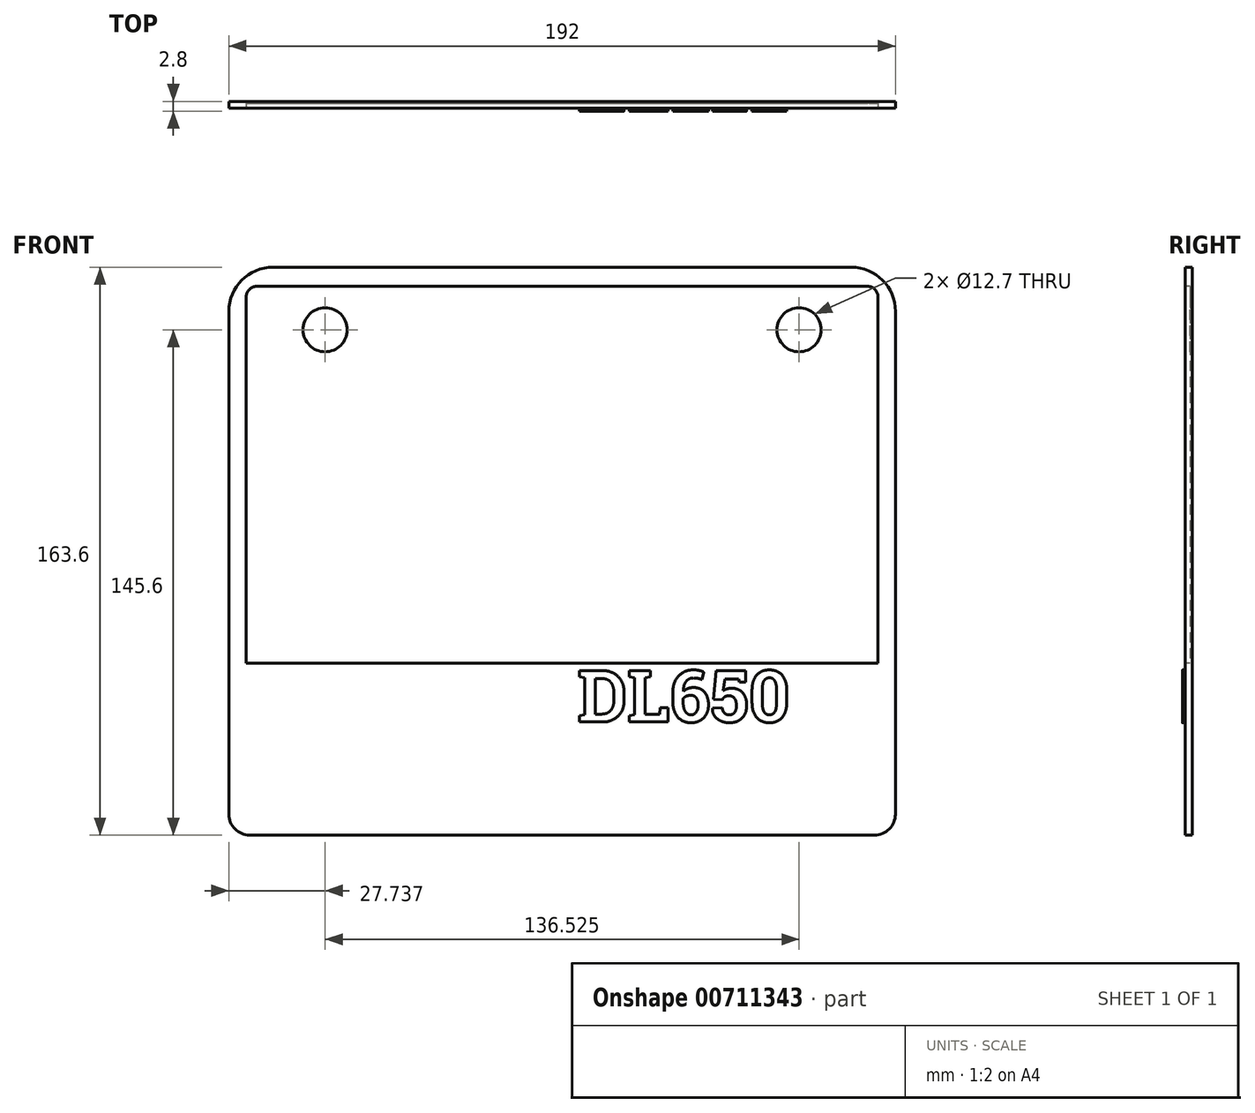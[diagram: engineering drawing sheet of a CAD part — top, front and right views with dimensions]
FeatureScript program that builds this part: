
annotation { "Feature Type Name" : "Feature", "Feature Type Description" : "" }
export const myFeature = defineFeature(function(context is Context, id is Id, definition is map)
    precondition{}
    {
        {
            var Q0;
            Q0=qCreatedBy(makeId("Front.planeOp"),FACE);
            var sketch = newSketch(context, id + "F0", { "sketchPlane" : qUnion([Q0])});
            skLineSegment(sketch, "E0", {"start": v(-83.3, 78) * mm, "end": v(83.3, 78) * mm});
            skLineSegment(sketch, "E1", {"start": v(-96, -23.6) * mm, "end": v(-96, 65.3) * mm});
            skLineSegment(sketch, "E2", {"start": v(96, 65.3) * mm, "end": v(96, -23.6) * mm});
            skCircle(sketch, "E3", {"center": v(-68.26, 60) * mm, "radius": 6.35 * mm});
            skCircle(sketch, "E4", {"center": v(68.26, 60) * mm, "radius": 6.35 * mm});
            skArc(sketch, "E5", {"start": v(-83.3, 78) * mm, "mid": v(-92.28, 74.28) * mm, "end": v(-96, 65.3) * mm});
            skArc(sketch, "E6", {"start": v(96, 65.3) * mm, "mid": v(92.28, 74.28) * mm, "end": v(83.3, 78) * mm});
            skLineSegment(sketch, "E7", {"start": v(-96, -23.6) * mm, "end": v(96, -23.6) * mm});
            skLineSegment(sketch, "E8", {"start": v(0, 78) * mm, "end": v(0, 44.35) * mm, "construction": true});
            skLineSegment(sketch, "E9", {"start": v(0, 0) * mm, "end": v(0, -23.6) * mm, "construction": true});
            skLineSegment(sketch, "E10", {"start": v(0, 44.35) * mm, "end": v(-96, 44.35) * mm, "construction": true});
            skLineSegment(sketch, "E11", {"start": v(0, 44.35) * mm, "end": v(96, 44.35) * mm, "construction": true});
            skSolve(sketch);
        }
        {
            var Q0;
            Q0=qSketchRegion(id+"F0",true);
            extrude(context, id + "F1", {"entities" : qUnion([Q0]), "depth" : 2 * mm, "offsetDistance" : 25 * mm});
        }
        {
            var Q0;
            Q0=makeQuery(id+"F1.opExtrude","CAP_FACE",FACE,{"disambiguationData":[OSD([sQuery(id+"F0.wireOp",EDGE,"E0"),sQuery(id+"F0.wireOp",EDGE,"48a6f060-a1ac-46d0-8047-a4f0a9823539"),sQuery(id+"F0.wireOp",EDGE,"E1"),sQuery(id+"F0.wireOp",EDGE,"E2"),sQuery(id+"F0.wireOp",EDGE,"f30ca258-66be-4d38-bb74-7f78c57f1080"),sQuery(id+"F0.wireOp",EDGE,"45272e1f-5984-409b-a4f0-3096130aef37"),sQuery(id+"F0.wireOp",EDGE,"648265e5-3534-4ccd-a4d5-83f80079090c"),sQuery(id+"F0.wireOp",EDGE,"c0985e6e-a1f7-4fb3-8751-1b5ac6839632"),sQuery(id+"F0.wireOp",EDGE,"e40d4cf7-7397-40ef-a449-90f8d66566dd"),sQuery(id+"F0.wireOp",EDGE,"e08eb2a6-f8ba-4677-9665-afa96b0a5c42"),sQuery(id+"F0.wireOp",EDGE,"e09e89fb-475b-45c4-a03c-8bf25691b274"),sQuery(id+"F0.wireOp",EDGE,"c3a1d90c-5dae-4514-9c18-9578f9fa1c24"),sQuery(id+"F0.wireOp",EDGE,"de0bfc80-6dc8-401c-842a-22218dc18f48"),sQuery(id+"F0.wireOp",EDGE,"10bace14-cf57-4a17-8dbc-91b2d8cd16bf"),sQuery(id+"F0.wireOp",EDGE,"deb3eb6b-2df6-45dd-ab49-f1686ca42383"),sQuery(id+"F0.wireOp",EDGE,"6de70d99-d249-41b2-88aa-bb0862796ce5"),sQuery(id+"F0.wireOp",EDGE,"b2971fcf-4c8f-4d95-a7b3-968699cf8065"),sQuery(id+"F0.wireOp",EDGE,"79488e33-7403-455a-a2d1-9183c7a7dc75"),sQuery(id+"F0.wireOp",EDGE,"aa5a9b35-dc5f-46a3-a21f-bc2f6a5ba8c3"),sQuery(id+"F0.wireOp",EDGE,"64001aba-4a60-4bdb-a6e0-b909cfa90190"),sQuery(id+"F0.wireOp",EDGE,"69a3c832-ee76-48c3-8be5-449944f03f95"),sQuery(id+"F0.wireOp",EDGE,"49a81c46-1861-4f30-adb0-815aeb534458"),sQuery(id+"F0.wireOp",EDGE,"e41367db-3de3-4109-90ef-63e5f0f7b1f7"),sQuery(id+"F0.wireOp",EDGE,"6e4c30f9-b3e7-4410-98fe-95563731d562"),sQuery(id+"F0.wireOp",EDGE,"50d6a7da-0eb8-46df-9db0-2777529e0e33"),sQuery(id+"F0.wireOp",EDGE,"8f5f6bae-5651-4266-a81d-530af63d2ea9"),sQuery(id+"F0.wireOp",EDGE,"0c91ba03-d5dc-41c7-8701-761e688114d9"),sQuery(id+"F0.wireOp",EDGE,"10e95849-eba9-4293-a9a6-05e2b37bbdfd"),sQuery(id+"F0.wireOp",EDGE,"edf70701-9639-44fa-8111-f0ba9ba4bb0e"),sQuery(id+"F0.wireOp",EDGE,"9cb7c61f-063f-4e49-a479-e91a873714ef"),sQuery(id+"F0.wireOp",EDGE,"23d4df54-0a09-4bbe-b8b9-fc41ac67f4ac"),sQuery(id+"F0.wireOp",EDGE,"d0cc7293-f9a2-43ae-ac4b-742a364b32c0"),sQuery(id+"F0.wireOp",EDGE,"1dbc8700-6e9f-4588-83ba-0a038fd47aa9"),sQuery(id+"F0.wireOp",EDGE,"171cbcd0-81c7-4dfe-8efe-28eec8b9f1e2"),sQuery(id+"F0.wireOp",EDGE,"1b840b68-42d4-491e-8676-f044272edf1d"),sQuery(id+"F0.wireOp",EDGE,"477a06df-0e00-41ca-87d7-5c34f2a07242"),sQuery(id+"F0.wireOp",EDGE,"7aeb2e31-d47a-4962-ad1a-87ad22c54afe"),sQuery(id+"F0.wireOp",EDGE,"8aeabe10-1c55-41c1-b53d-efc54e2343e8"),sQuery(id+"F0.wireOp",EDGE,"56056688-4674-4c79-9f3a-c66bce5d7240"),sQuery(id+"F0.wireOp",EDGE,"2ba6e904-2303-4a58-a2cc-d8b69b776228"),sQuery(id+"F0.wireOp",EDGE,"5e924ffd-c203-416b-82ef-407f079c669c"),sQuery(id+"F0.wireOp",EDGE,"22999e4d-675b-4f8e-a222-469bac07e6be"),sQuery(id+"F0.wireOp",EDGE,"8f11fb03-c33d-4eef-9f43-5a4f08b6129f"),sQuery(id+"F0.wireOp",EDGE,"a5862e19-85fe-4436-8071-eee2bcb2075c"),sQuery(id+"F0.wireOp",EDGE,"ed11b90d-34d2-40d8-97b3-85c497fa4b90"),sQuery(id+"F0.wireOp",EDGE,"8821150d-f62d-464a-944b-e17730e76b97"),sQuery(id+"F0.wireOp",EDGE,"73421591-e8bf-419b-8db1-77e700152255"),sQuery(id+"F0.wireOp",EDGE,"55a8d366-2669-4621-9984-ea7371f670e7"),sQuery(id+"F0.wireOp",EDGE,"fca3974c-c5bd-4598-b391-3bcec77630d6"),sQuery(id+"F0.wireOp",EDGE,"1c73d825-d1c4-4b0e-8cd0-2f197b32ed0e"),sQuery(id+"F0.wireOp",EDGE,"f12474dd-ca9d-467a-b6b7-96876f0ada5b"),sQuery(id+"F0.wireOp",EDGE,"ffd498c9-8f44-4c4b-88ae-d53ebce42681"),sQuery(id+"F0.wireOp",EDGE,"d78736cb-32b1-4983-8c7f-334d7760df66"),sQuery(id+"F0.wireOp",EDGE,"95740ca0-fcd5-4cb7-9504-a285a5dde6e3"),sQuery(id+"F0.wireOp",EDGE,"ebb5eec3-1149-4952-a6d1-94870ff9836f"),sQuery(id+"F0.wireOp",EDGE,"09364745-caed-4ffe-8d3c-952926bc9417"),sQuery(id+"F0.wireOp",EDGE,"a9181265-9252-4b23-9b63-f6bef6a5911b"),sQuery(id+"F0.wireOp",EDGE,"a53fe2a5-8e1d-4d15-8c4a-13980fa5923c"),sQuery(id+"F0.wireOp",EDGE,"9b227ee3-73b3-485d-a44c-8cd02b23a3f0"),sQuery(id+"F0.wireOp",EDGE,"062db7e1-9f89-4046-92a1-9e257b0f6c50"),sQuery(id+"F0.wireOp",EDGE,"351c1721-7ed2-435b-ad4a-6d0b63d51eff"),sQuery(id+"F0.wireOp",EDGE,"71a8f4bf-e319-473b-8b4e-3c091c66e44c"),sQuery(id+"F0.wireOp",EDGE,"c68ce1a5-2e28-4d52-a029-c52856a99a74"),sQuery(id+"F0.wireOp",EDGE,"561223bc-eb1b-49aa-80b6-663cd7c405cc"),sQuery(id+"F0.wireOp",EDGE,"4449a819-5709-48c0-965c-65add78f8043"),sQuery(id+"F0.wireOp",EDGE,"a0f13820-d3c8-4b17-b0b8-00fd948fe85f"),sQuery(id+"F0.wireOp",EDGE,"20fca5f8-8561-4aa7-a30f-3738d70a8836"),sQuery(id+"F0.wireOp",EDGE,"920726d8-d7a8-4d7b-bd5a-44d794fb4a9e"),sQuery(id+"F0.wireOp",EDGE,"a76c174e-0144-4079-be69-9e1200ad9bf8"),sQuery(id+"F0.wireOp",EDGE,"98b53387-61df-4284-a1fd-1e532390bc76"),sQuery(id+"F0.wireOp",EDGE,"7970af7d-46bf-4ec9-b671-f062ccba2269"),sQuery(id+"F0.wireOp",EDGE,"6e09d304-04a0-4725-848f-3effe17a6afc"),sQuery(id+"F0.wireOp",EDGE,"3df50d65-f073-4170-bc94-899382cb2db7"),sQuery(id+"F0.wireOp",EDGE,"ec83f8f2-8803-4207-88f9-0d4175c8ecd2"),sQuery(id+"F0.wireOp",EDGE,"2f88a13a-97f7-4f31-871f-ef8b0bef47c0"),sQuery(id+"F0.wireOp",EDGE,"06910b89-3a32-40f6-98a8-ac0792bcf854"),sQuery(id+"F0.wireOp",EDGE,"1496428c-a744-4ad0-9076-c4c48af7c995"),sQuery(id+"F0.wireOp",EDGE,"cc24b7ec-eed3-4d97-bc37-77a5319da4e8"),sQuery(id+"F0.wireOp",EDGE,"f009715c-78f4-41d5-a120-40e9715128f4"),sQuery(id+"F0.wireOp",EDGE,"5595ca81-0dc4-4751-825f-2c64607c6bfd"),sQuery(id+"F0.wireOp",EDGE,"75137ea1-8823-43c0-92ee-8dea83bb2410"),sQuery(id+"F0.wireOp",EDGE,"f83aa6e6-86ae-462f-9473-6b6f0fb29268"),sQuery(id+"F0.wireOp",EDGE,"d90fdb54-86cb-4136-93d7-04ef30efafac"),sQuery(id+"F0.wireOp",EDGE,"8bd12bbf-22fc-44f8-9b72-60e51806dfd9"),sQuery(id+"F0.wireOp",EDGE,"d2235da4-86d1-4fb2-9421-07340d50dd9e"),sQuery(id+"F0.wireOp",EDGE,"63672669-45e7-48f5-b998-5c0e149c1244"),sQuery(id+"F0.wireOp",EDGE,"58c0fe2c-0100-4913-a047-5c3918bec01d"),sQuery(id+"F0.wireOp",EDGE,"41e70165-0540-472b-ae5f-d4663d4ebe0f"),sQuery(id+"F0.wireOp",EDGE,"6970c7cc-29ee-40f8-b0b1-14e57c32c814"),sQuery(id+"F0.wireOp",EDGE,"349e1bc8-b4a3-4d58-8a14-12c9859b9f7c"),sQuery(id+"F0.wireOp",EDGE,"87991a84-08ac-46d3-90c5-f5fa6d0c5a83"),sQuery(id+"F0.wireOp",EDGE,"d48f1f7f-ed81-45d4-8615-b0910d7520c1"),sQuery(id+"F0.wireOp",EDGE,"7e9c43bc-bf7d-4118-b5fc-4f360d9f3191"),sQuery(id+"F0.wireOp",EDGE,"2759085c-90ad-42ab-8a63-b83350e672f3"),sQuery(id+"F0.wireOp",EDGE,"39805100-74d7-4eed-b193-147db33826ff"),sQuery(id+"F0.wireOp",EDGE,"6fa17770-5563-4e58-b27d-c8ec50f6b9eb"),sQuery(id+"F0.wireOp",EDGE,"32f67bb0-8620-4629-98bb-09f92e1a7203"),sQuery(id+"F0.wireOp",EDGE,"1ab79bf1-ba5c-4050-a713-1e5aa506e06c"),sQuery(id+"F0.wireOp",EDGE,"ffed6f08-e811-4981-a8fd-a7a3ecd42359"),sQuery(id+"F0.wireOp",EDGE,"2f2290aa-816a-4cc3-8e39-136d9264129f"),sQuery(id+"F0.wireOp",EDGE,"b78c8009-cc0b-41b3-a308-2ea56fda7653"),sQuery(id+"F0.wireOp",EDGE,"19267ec7-4eb6-4897-a0c4-8a92806a641a"),sQuery(id+"F0.wireOp",EDGE,"d0838ca9-0bd1-4f24-9d56-d46021ac47bb"),sQuery(id+"F0.wireOp",EDGE,"ce547bf3-1506-4fd9-949b-1fb36aabb9ca"),sQuery(id+"F0.wireOp",EDGE,"e414b3ae-820b-420c-b87e-729e0b5eba94"),sQuery(id+"F0.wireOp",EDGE,"edeb106c-0092-4fe6-b9c2-1a1c4f8eb62e"),sQuery(id+"F0.wireOp",EDGE,"c81b4543-384f-45e1-8dd5-319bf77e4dd3"),sQuery(id+"F0.wireOp",EDGE,"46d69cc5-4e9e-43d0-9594-28f258b2da8d"),sQuery(id+"F0.wireOp",EDGE,"0f81ca49-7ceb-4d09-8dc9-9a04f8bc6888"),sQuery(id+"F0.wireOp",EDGE,"b58b9564-60eb-4c8a-b30f-9b977b1b8378"),sQuery(id+"F0.wireOp",EDGE,"d8bbd356-4e6d-4438-af8e-85043a16574a"),sQuery(id+"F0.wireOp",EDGE,"95fa0bd5-89c6-4184-a0ff-f4c07d22a4ae"),sQuery(id+"F0.wireOp",EDGE,"f4548e74-734f-430b-9c25-dfe130f893d1"),sQuery(id+"F0.wireOp",EDGE,"aa9bd5ec-27bf-46b3-b434-4e99c0207ced"),sQuery(id+"F0.wireOp",EDGE,"9be34343-3f5a-40f5-8c55-a74b86983d61"),sQuery(id+"F0.wireOp",EDGE,"78e4d226-de00-4f6e-ab81-cb0a13cdacba"),sQuery(id+"F0.wireOp",EDGE,"3a4dbe18-ff8c-426a-b249-17c5fc8cdc1d"),sQuery(id+"F0.wireOp",EDGE,"1aed8480-7217-479a-a0ab-f2862b378fde"),sQuery(id+"F0.wireOp",EDGE,"b4489634-a053-4e93-951f-f30401c3c6f6"),sQuery(id+"F0.wireOp",EDGE,"cc371cea-5bb3-4e27-997b-0d34cdc5a024"),sQuery(id+"F0.wireOp",EDGE,"86368e5d-c637-4ae6-8edd-554a0b5499c9"),sQuery(id+"F0.wireOp",EDGE,"13f25098-72eb-41f9-be21-613ca2679d4b"),sQuery(id+"F0.wireOp",EDGE,"1f474f0c-89c3-40ee-8296-02d5ac8c763d"),sQuery(id+"F0.wireOp",EDGE,"13320aed-ccdc-4340-973a-86da583243d3"),sQuery(id+"F0.wireOp",EDGE,"0f343cd8-6904-487c-9847-16acd28769b1"),sQuery(id+"F0.wireOp",EDGE,"f8d5171c-c807-4338-b4d2-ff111a4d6950"),sQuery(id+"F0.wireOp",EDGE,"531f2c4b-3846-4b77-b256-c3f1f96e1e9d"),sQuery(id+"F0.wireOp",EDGE,"f1731d2a-7704-4802-8ffe-e10816912d59"),sQuery(id+"F0.wireOp",EDGE,"663e4867-d1df-44f6-8d72-edf692fa190b"),sQuery(id+"F0.wireOp",EDGE,"ab6ac0ee-4fb0-40ab-99bd-49c6310301f1"),sQuery(id+"F0.wireOp",EDGE,"020361ae-c990-440f-b82b-d8defa8b7b3c"),sQuery(id+"F0.wireOp",EDGE,"f234d57d-ff2e-4084-99c6-6c5da22014f4"),sQuery(id+"F0.wireOp",EDGE,"5704d1bf-8f80-4d6a-bd46-ef1de08cc11a"),sQuery(id+"F0.wireOp",EDGE,"49977618-c097-4a49-a1ed-c88bfdf155e3"),sQuery(id+"F0.wireOp",EDGE,"ba9d945f-4033-4ba8-a865-6404f0a478a9"),sQuery(id+"F0.wireOp",EDGE,"c57414d4-a29c-435f-b64d-f2822a14b6a6"),sQuery(id+"F0.wireOp",EDGE,"be5730e7-9658-4d88-be84-16e7c03488bd"),sQuery(id+"F0.wireOp",EDGE,"a75bae47-d3a2-4152-ab54-74ed0c49e5a7"),sQuery(id+"F0.wireOp",EDGE,"6e3ff476-3da9-4782-8826-f396f37c11b6"),sQuery(id+"F0.wireOp",EDGE,"05769db6-19a1-4fe3-98a5-9d1978582ff3"),sQuery(id+"F0.wireOp",EDGE,"5dad99bb-ebf8-4bc1-8dc4-4c0a6e99aceb"),sQuery(id+"F0.wireOp",EDGE,"c816ae48-71c4-4d0e-8c30-5d1046f78968"),sQuery(id+"F0.wireOp",EDGE,"cfd27d30-f5e3-48dc-9665-aa6919d9858b"),sQuery(id+"F0.wireOp",EDGE,"4725fb37-e1ea-4f57-b98a-89feef752827"),sQuery(id+"F0.wireOp",EDGE,"ae6adbf3-7d98-4c9e-8eb2-f79f6d337834"),sQuery(id+"F0.wireOp",EDGE,"640fbc53-f186-4556-84a7-69dc03839d6f"),sQuery(id+"F0.wireOp",EDGE,"e1422021-42bf-4d48-97a0-4a21d4969dc9"),sQuery(id+"F0.wireOp",EDGE,"c074cf32-69e8-4938-8c1f-45b8d0bb0a1c"),sQuery(id+"F0.wireOp",EDGE,"a8cc22a8-0297-4380-896a-58e0a4d64946"),sQuery(id+"F0.wireOp",EDGE,"2896c270-dc6a-46f7-af7e-f09f457604b9"),sQuery(id+"F0.wireOp",EDGE,"f6aba6df-df45-4b05-993e-c7defc46a8a9"),sQuery(id+"F0.wireOp",EDGE,"8d709430-df8d-444d-80f1-d8a9d8f49d36"),sQuery(id+"F0.wireOp",EDGE,"157fc770-0e9c-4f22-853e-0631539bb4e1"),sQuery(id+"F0.wireOp",EDGE,"a9f1098b-83a8-4a87-b43b-ebdedd82ef22"),sQuery(id+"F0.wireOp",EDGE,"aa613513-3a1a-4f7c-8e9e-b6ef198c339f"),sQuery(id+"F0.wireOp",EDGE,"fe532b5b-20c2-4205-9ddd-15005d39a7ff"),sQuery(id+"F0.wireOp",EDGE,"65eb4da6-f79f-4cfa-8aa6-be833dba4871"),sQuery(id+"F0.wireOp",EDGE,"c5a74e05-6458-4890-878c-c1706ed33956"),sQuery(id+"F0.wireOp",EDGE,"496d6b06-fe4e-4fad-814f-3270d9f86b10"),sQuery(id+"F0.wireOp",EDGE,"e228dba5-c171-4fc2-b486-8333351927fa"),sQuery(id+"F0.wireOp",EDGE,"d01ee6cb-36a2-45a1-89ac-166ec7de60b6"),sQuery(id+"F0.wireOp",EDGE,"E3"),sQuery(id+"F0.wireOp",EDGE,"E4"),sQuery(id+"F0.wireOp",EDGE,"436595a8-e4a6-4182-82a2-6fdc5edbe3d4"),sQuery(id+"F0.wireOp",EDGE,"6fa8d768-685f-4659-b18a-b4b0655affab"),sQuery(id+"F0.wireOp",EDGE,"3112937d-f164-4bee-b1b8-f487c5c27332"),sQuery(id+"F0.wireOp",EDGE,"2838ab75-a7b3-46be-88fa-19408c43f44a"),sQuery(id+"F0.wireOp",EDGE,"4df78863-24a2-4663-8bca-78eb0f9ee46f"),sQuery(id+"F0.wireOp",EDGE,"76a8d0a0-a03e-4017-96cb-accdf860527a"),sQuery(id+"F0.wireOp",EDGE,"d24411e6-fbae-4226-8ade-65dde889be9d"),sQuery(id+"F0.wireOp",EDGE,"bc01f53f-b851-4eac-bdc6-b53b8c4c76a6"),sQuery(id+"F0.wireOp",EDGE,"69d3b90a-bc34-4f77-bf78-b3aee6b0a92d"),sQuery(id+"F0.wireOp",EDGE,"373f017d-76e3-442f-9662-ada9d0238173"),sQuery(id+"F0.wireOp",EDGE,"E5"),sQuery(id+"F0.wireOp",EDGE,"E6"),sQuery(id+"F0.wireOp",EDGE,"E7"),sQuery(id+"F0.wireOp",EDGE,"2cd16a8c-3307-4928-bd26-f5d255e7399a"),sQuery(id+"F0.wireOp",EDGE,"193ac13c-8e04-4e5c-91c6-e2d340e07c24"),sQuery(id+"F0.wireOp",EDGE,"6f13a96e-32fe-4fc2-9d82-1492d29b6e04"),sQuery(id+"F0.wireOp",EDGE,"fc8c22b4-d4e1-4527-bd38-377e5530003c"),sQuery(id+"F0.wireOp",EDGE,"4d59d710-4fe3-4597-a13d-8c3004e22d5d"),sQuery(id+"F0.wireOp",EDGE,"29ced08f-bc4c-4871-942e-da1849301c59"),sQuery(id+"F0.wireOp",EDGE,"5d328fcf-ca32-4b9a-8d95-4cec8a7c74f5"),sQuery(id+"F0.wireOp",EDGE,"I1ITQqyg-hlTV-tP51-8M3V-AqXVVhc1bbyB"),sQuery(id+"F0.wireOp",EDGE,"Ww1sCOVc-raFa-45lX-seSL-zmaeCrGf7sdz")])],"isStart":false});
            var sketch = newSketch(context, id + "F2", { "sketchPlane" : qUnion([Q0])});
            skLineSegment(sketch, "E12.bottom", {"start": v(-96, -23.6) * mm, "end": v(96, -23.6) * mm});
            skLineSegment(sketch, "E12.top", {"start": v(-90, -85.6) * mm, "end": v(90, -85.6) * mm});
            skLineSegment(sketch, "E12.left", {"start": v(-96, -23.6) * mm, "end": v(-96, -79.6) * mm});
            skLineSegment(sketch, "E12.right", {"start": v(96, -23.6) * mm, "end": v(96, -79.6) * mm});
            skPoint(sketch, "E13.visualSharp", {"position": v(-96, -85.6) * mm});
            skArc(sketch, "E13.filletArc", {"start": v(-96, -79.6) * mm, "mid": v(-94.24, -83.84) * mm, "end": v(-90, -85.6) * mm});
            skPoint(sketch, "E14.visualSharp", {"position": v(96, -85.6) * mm});
            skArc(sketch, "E14.filletArc", {"start": v(90, -85.6) * mm, "mid": v(94.24, -83.84) * mm, "end": v(96, -79.6) * mm});
            skSolve(sketch);
        }
        {
            var Q0;
            Q0=qSketchRegion(id+"F2",true);
            var Q1;
            Q1=makeQuery(id+"F1.opExtrude","CAP_FACE",FACE,{"disambiguationData":[OSD([sQuery(id+"F0.wireOp",EDGE,"E0"),sQuery(id+"F0.wireOp",EDGE,"48a6f060-a1ac-46d0-8047-a4f0a9823539"),sQuery(id+"F0.wireOp",EDGE,"E1"),sQuery(id+"F0.wireOp",EDGE,"E2"),sQuery(id+"F0.wireOp",EDGE,"f30ca258-66be-4d38-bb74-7f78c57f1080"),sQuery(id+"F0.wireOp",EDGE,"45272e1f-5984-409b-a4f0-3096130aef37"),sQuery(id+"F0.wireOp",EDGE,"648265e5-3534-4ccd-a4d5-83f80079090c"),sQuery(id+"F0.wireOp",EDGE,"c0985e6e-a1f7-4fb3-8751-1b5ac6839632"),sQuery(id+"F0.wireOp",EDGE,"e40d4cf7-7397-40ef-a449-90f8d66566dd"),sQuery(id+"F0.wireOp",EDGE,"e08eb2a6-f8ba-4677-9665-afa96b0a5c42"),sQuery(id+"F0.wireOp",EDGE,"e09e89fb-475b-45c4-a03c-8bf25691b274"),sQuery(id+"F0.wireOp",EDGE,"c3a1d90c-5dae-4514-9c18-9578f9fa1c24"),sQuery(id+"F0.wireOp",EDGE,"de0bfc80-6dc8-401c-842a-22218dc18f48"),sQuery(id+"F0.wireOp",EDGE,"10bace14-cf57-4a17-8dbc-91b2d8cd16bf"),sQuery(id+"F0.wireOp",EDGE,"deb3eb6b-2df6-45dd-ab49-f1686ca42383"),sQuery(id+"F0.wireOp",EDGE,"6de70d99-d249-41b2-88aa-bb0862796ce5"),sQuery(id+"F0.wireOp",EDGE,"b2971fcf-4c8f-4d95-a7b3-968699cf8065"),sQuery(id+"F0.wireOp",EDGE,"79488e33-7403-455a-a2d1-9183c7a7dc75"),sQuery(id+"F0.wireOp",EDGE,"aa5a9b35-dc5f-46a3-a21f-bc2f6a5ba8c3"),sQuery(id+"F0.wireOp",EDGE,"64001aba-4a60-4bdb-a6e0-b909cfa90190"),sQuery(id+"F0.wireOp",EDGE,"69a3c832-ee76-48c3-8be5-449944f03f95"),sQuery(id+"F0.wireOp",EDGE,"49a81c46-1861-4f30-adb0-815aeb534458"),sQuery(id+"F0.wireOp",EDGE,"e41367db-3de3-4109-90ef-63e5f0f7b1f7"),sQuery(id+"F0.wireOp",EDGE,"6e4c30f9-b3e7-4410-98fe-95563731d562"),sQuery(id+"F0.wireOp",EDGE,"50d6a7da-0eb8-46df-9db0-2777529e0e33"),sQuery(id+"F0.wireOp",EDGE,"8f5f6bae-5651-4266-a81d-530af63d2ea9"),sQuery(id+"F0.wireOp",EDGE,"0c91ba03-d5dc-41c7-8701-761e688114d9"),sQuery(id+"F0.wireOp",EDGE,"10e95849-eba9-4293-a9a6-05e2b37bbdfd"),sQuery(id+"F0.wireOp",EDGE,"edf70701-9639-44fa-8111-f0ba9ba4bb0e"),sQuery(id+"F0.wireOp",EDGE,"9cb7c61f-063f-4e49-a479-e91a873714ef"),sQuery(id+"F0.wireOp",EDGE,"23d4df54-0a09-4bbe-b8b9-fc41ac67f4ac"),sQuery(id+"F0.wireOp",EDGE,"d0cc7293-f9a2-43ae-ac4b-742a364b32c0"),sQuery(id+"F0.wireOp",EDGE,"1dbc8700-6e9f-4588-83ba-0a038fd47aa9"),sQuery(id+"F0.wireOp",EDGE,"171cbcd0-81c7-4dfe-8efe-28eec8b9f1e2"),sQuery(id+"F0.wireOp",EDGE,"1b840b68-42d4-491e-8676-f044272edf1d"),sQuery(id+"F0.wireOp",EDGE,"477a06df-0e00-41ca-87d7-5c34f2a07242"),sQuery(id+"F0.wireOp",EDGE,"7aeb2e31-d47a-4962-ad1a-87ad22c54afe"),sQuery(id+"F0.wireOp",EDGE,"8aeabe10-1c55-41c1-b53d-efc54e2343e8"),sQuery(id+"F0.wireOp",EDGE,"56056688-4674-4c79-9f3a-c66bce5d7240"),sQuery(id+"F0.wireOp",EDGE,"2ba6e904-2303-4a58-a2cc-d8b69b776228"),sQuery(id+"F0.wireOp",EDGE,"5e924ffd-c203-416b-82ef-407f079c669c"),sQuery(id+"F0.wireOp",EDGE,"22999e4d-675b-4f8e-a222-469bac07e6be"),sQuery(id+"F0.wireOp",EDGE,"8f11fb03-c33d-4eef-9f43-5a4f08b6129f"),sQuery(id+"F0.wireOp",EDGE,"a5862e19-85fe-4436-8071-eee2bcb2075c"),sQuery(id+"F0.wireOp",EDGE,"ed11b90d-34d2-40d8-97b3-85c497fa4b90"),sQuery(id+"F0.wireOp",EDGE,"8821150d-f62d-464a-944b-e17730e76b97"),sQuery(id+"F0.wireOp",EDGE,"73421591-e8bf-419b-8db1-77e700152255"),sQuery(id+"F0.wireOp",EDGE,"55a8d366-2669-4621-9984-ea7371f670e7"),sQuery(id+"F0.wireOp",EDGE,"fca3974c-c5bd-4598-b391-3bcec77630d6"),sQuery(id+"F0.wireOp",EDGE,"1c73d825-d1c4-4b0e-8cd0-2f197b32ed0e"),sQuery(id+"F0.wireOp",EDGE,"f12474dd-ca9d-467a-b6b7-96876f0ada5b"),sQuery(id+"F0.wireOp",EDGE,"ffd498c9-8f44-4c4b-88ae-d53ebce42681"),sQuery(id+"F0.wireOp",EDGE,"d78736cb-32b1-4983-8c7f-334d7760df66"),sQuery(id+"F0.wireOp",EDGE,"95740ca0-fcd5-4cb7-9504-a285a5dde6e3"),sQuery(id+"F0.wireOp",EDGE,"ebb5eec3-1149-4952-a6d1-94870ff9836f"),sQuery(id+"F0.wireOp",EDGE,"09364745-caed-4ffe-8d3c-952926bc9417"),sQuery(id+"F0.wireOp",EDGE,"a9181265-9252-4b23-9b63-f6bef6a5911b"),sQuery(id+"F0.wireOp",EDGE,"a53fe2a5-8e1d-4d15-8c4a-13980fa5923c"),sQuery(id+"F0.wireOp",EDGE,"9b227ee3-73b3-485d-a44c-8cd02b23a3f0"),sQuery(id+"F0.wireOp",EDGE,"062db7e1-9f89-4046-92a1-9e257b0f6c50"),sQuery(id+"F0.wireOp",EDGE,"351c1721-7ed2-435b-ad4a-6d0b63d51eff"),sQuery(id+"F0.wireOp",EDGE,"71a8f4bf-e319-473b-8b4e-3c091c66e44c"),sQuery(id+"F0.wireOp",EDGE,"c68ce1a5-2e28-4d52-a029-c52856a99a74"),sQuery(id+"F0.wireOp",EDGE,"561223bc-eb1b-49aa-80b6-663cd7c405cc"),sQuery(id+"F0.wireOp",EDGE,"4449a819-5709-48c0-965c-65add78f8043"),sQuery(id+"F0.wireOp",EDGE,"a0f13820-d3c8-4b17-b0b8-00fd948fe85f"),sQuery(id+"F0.wireOp",EDGE,"20fca5f8-8561-4aa7-a30f-3738d70a8836"),sQuery(id+"F0.wireOp",EDGE,"920726d8-d7a8-4d7b-bd5a-44d794fb4a9e"),sQuery(id+"F0.wireOp",EDGE,"a76c174e-0144-4079-be69-9e1200ad9bf8"),sQuery(id+"F0.wireOp",EDGE,"98b53387-61df-4284-a1fd-1e532390bc76"),sQuery(id+"F0.wireOp",EDGE,"7970af7d-46bf-4ec9-b671-f062ccba2269"),sQuery(id+"F0.wireOp",EDGE,"6e09d304-04a0-4725-848f-3effe17a6afc"),sQuery(id+"F0.wireOp",EDGE,"3df50d65-f073-4170-bc94-899382cb2db7"),sQuery(id+"F0.wireOp",EDGE,"ec83f8f2-8803-4207-88f9-0d4175c8ecd2"),sQuery(id+"F0.wireOp",EDGE,"2f88a13a-97f7-4f31-871f-ef8b0bef47c0"),sQuery(id+"F0.wireOp",EDGE,"06910b89-3a32-40f6-98a8-ac0792bcf854"),sQuery(id+"F0.wireOp",EDGE,"1496428c-a744-4ad0-9076-c4c48af7c995"),sQuery(id+"F0.wireOp",EDGE,"cc24b7ec-eed3-4d97-bc37-77a5319da4e8"),sQuery(id+"F0.wireOp",EDGE,"f009715c-78f4-41d5-a120-40e9715128f4"),sQuery(id+"F0.wireOp",EDGE,"5595ca81-0dc4-4751-825f-2c64607c6bfd"),sQuery(id+"F0.wireOp",EDGE,"75137ea1-8823-43c0-92ee-8dea83bb2410"),sQuery(id+"F0.wireOp",EDGE,"f83aa6e6-86ae-462f-9473-6b6f0fb29268"),sQuery(id+"F0.wireOp",EDGE,"d90fdb54-86cb-4136-93d7-04ef30efafac"),sQuery(id+"F0.wireOp",EDGE,"8bd12bbf-22fc-44f8-9b72-60e51806dfd9"),sQuery(id+"F0.wireOp",EDGE,"d2235da4-86d1-4fb2-9421-07340d50dd9e"),sQuery(id+"F0.wireOp",EDGE,"63672669-45e7-48f5-b998-5c0e149c1244"),sQuery(id+"F0.wireOp",EDGE,"58c0fe2c-0100-4913-a047-5c3918bec01d"),sQuery(id+"F0.wireOp",EDGE,"41e70165-0540-472b-ae5f-d4663d4ebe0f"),sQuery(id+"F0.wireOp",EDGE,"6970c7cc-29ee-40f8-b0b1-14e57c32c814"),sQuery(id+"F0.wireOp",EDGE,"349e1bc8-b4a3-4d58-8a14-12c9859b9f7c"),sQuery(id+"F0.wireOp",EDGE,"87991a84-08ac-46d3-90c5-f5fa6d0c5a83"),sQuery(id+"F0.wireOp",EDGE,"d48f1f7f-ed81-45d4-8615-b0910d7520c1"),sQuery(id+"F0.wireOp",EDGE,"7e9c43bc-bf7d-4118-b5fc-4f360d9f3191"),sQuery(id+"F0.wireOp",EDGE,"2759085c-90ad-42ab-8a63-b83350e672f3"),sQuery(id+"F0.wireOp",EDGE,"39805100-74d7-4eed-b193-147db33826ff"),sQuery(id+"F0.wireOp",EDGE,"6fa17770-5563-4e58-b27d-c8ec50f6b9eb"),sQuery(id+"F0.wireOp",EDGE,"32f67bb0-8620-4629-98bb-09f92e1a7203"),sQuery(id+"F0.wireOp",EDGE,"1ab79bf1-ba5c-4050-a713-1e5aa506e06c"),sQuery(id+"F0.wireOp",EDGE,"ffed6f08-e811-4981-a8fd-a7a3ecd42359"),sQuery(id+"F0.wireOp",EDGE,"2f2290aa-816a-4cc3-8e39-136d9264129f"),sQuery(id+"F0.wireOp",EDGE,"b78c8009-cc0b-41b3-a308-2ea56fda7653"),sQuery(id+"F0.wireOp",EDGE,"19267ec7-4eb6-4897-a0c4-8a92806a641a"),sQuery(id+"F0.wireOp",EDGE,"d0838ca9-0bd1-4f24-9d56-d46021ac47bb"),sQuery(id+"F0.wireOp",EDGE,"ce547bf3-1506-4fd9-949b-1fb36aabb9ca"),sQuery(id+"F0.wireOp",EDGE,"e414b3ae-820b-420c-b87e-729e0b5eba94"),sQuery(id+"F0.wireOp",EDGE,"edeb106c-0092-4fe6-b9c2-1a1c4f8eb62e"),sQuery(id+"F0.wireOp",EDGE,"c81b4543-384f-45e1-8dd5-319bf77e4dd3"),sQuery(id+"F0.wireOp",EDGE,"46d69cc5-4e9e-43d0-9594-28f258b2da8d"),sQuery(id+"F0.wireOp",EDGE,"0f81ca49-7ceb-4d09-8dc9-9a04f8bc6888"),sQuery(id+"F0.wireOp",EDGE,"b58b9564-60eb-4c8a-b30f-9b977b1b8378"),sQuery(id+"F0.wireOp",EDGE,"d8bbd356-4e6d-4438-af8e-85043a16574a"),sQuery(id+"F0.wireOp",EDGE,"95fa0bd5-89c6-4184-a0ff-f4c07d22a4ae"),sQuery(id+"F0.wireOp",EDGE,"f4548e74-734f-430b-9c25-dfe130f893d1"),sQuery(id+"F0.wireOp",EDGE,"aa9bd5ec-27bf-46b3-b434-4e99c0207ced"),sQuery(id+"F0.wireOp",EDGE,"9be34343-3f5a-40f5-8c55-a74b86983d61"),sQuery(id+"F0.wireOp",EDGE,"78e4d226-de00-4f6e-ab81-cb0a13cdacba"),sQuery(id+"F0.wireOp",EDGE,"3a4dbe18-ff8c-426a-b249-17c5fc8cdc1d"),sQuery(id+"F0.wireOp",EDGE,"1aed8480-7217-479a-a0ab-f2862b378fde"),sQuery(id+"F0.wireOp",EDGE,"b4489634-a053-4e93-951f-f30401c3c6f6"),sQuery(id+"F0.wireOp",EDGE,"cc371cea-5bb3-4e27-997b-0d34cdc5a024"),sQuery(id+"F0.wireOp",EDGE,"86368e5d-c637-4ae6-8edd-554a0b5499c9"),sQuery(id+"F0.wireOp",EDGE,"13f25098-72eb-41f9-be21-613ca2679d4b"),sQuery(id+"F0.wireOp",EDGE,"1f474f0c-89c3-40ee-8296-02d5ac8c763d"),sQuery(id+"F0.wireOp",EDGE,"13320aed-ccdc-4340-973a-86da583243d3"),sQuery(id+"F0.wireOp",EDGE,"0f343cd8-6904-487c-9847-16acd28769b1"),sQuery(id+"F0.wireOp",EDGE,"f8d5171c-c807-4338-b4d2-ff111a4d6950"),sQuery(id+"F0.wireOp",EDGE,"531f2c4b-3846-4b77-b256-c3f1f96e1e9d"),sQuery(id+"F0.wireOp",EDGE,"f1731d2a-7704-4802-8ffe-e10816912d59"),sQuery(id+"F0.wireOp",EDGE,"663e4867-d1df-44f6-8d72-edf692fa190b"),sQuery(id+"F0.wireOp",EDGE,"ab6ac0ee-4fb0-40ab-99bd-49c6310301f1"),sQuery(id+"F0.wireOp",EDGE,"020361ae-c990-440f-b82b-d8defa8b7b3c"),sQuery(id+"F0.wireOp",EDGE,"f234d57d-ff2e-4084-99c6-6c5da22014f4"),sQuery(id+"F0.wireOp",EDGE,"5704d1bf-8f80-4d6a-bd46-ef1de08cc11a"),sQuery(id+"F0.wireOp",EDGE,"49977618-c097-4a49-a1ed-c88bfdf155e3"),sQuery(id+"F0.wireOp",EDGE,"ba9d945f-4033-4ba8-a865-6404f0a478a9"),sQuery(id+"F0.wireOp",EDGE,"c57414d4-a29c-435f-b64d-f2822a14b6a6"),sQuery(id+"F0.wireOp",EDGE,"be5730e7-9658-4d88-be84-16e7c03488bd"),sQuery(id+"F0.wireOp",EDGE,"a75bae47-d3a2-4152-ab54-74ed0c49e5a7"),sQuery(id+"F0.wireOp",EDGE,"6e3ff476-3da9-4782-8826-f396f37c11b6"),sQuery(id+"F0.wireOp",EDGE,"05769db6-19a1-4fe3-98a5-9d1978582ff3"),sQuery(id+"F0.wireOp",EDGE,"5dad99bb-ebf8-4bc1-8dc4-4c0a6e99aceb"),sQuery(id+"F0.wireOp",EDGE,"c816ae48-71c4-4d0e-8c30-5d1046f78968"),sQuery(id+"F0.wireOp",EDGE,"cfd27d30-f5e3-48dc-9665-aa6919d9858b"),sQuery(id+"F0.wireOp",EDGE,"4725fb37-e1ea-4f57-b98a-89feef752827"),sQuery(id+"F0.wireOp",EDGE,"ae6adbf3-7d98-4c9e-8eb2-f79f6d337834"),sQuery(id+"F0.wireOp",EDGE,"640fbc53-f186-4556-84a7-69dc03839d6f"),sQuery(id+"F0.wireOp",EDGE,"e1422021-42bf-4d48-97a0-4a21d4969dc9"),sQuery(id+"F0.wireOp",EDGE,"c074cf32-69e8-4938-8c1f-45b8d0bb0a1c"),sQuery(id+"F0.wireOp",EDGE,"a8cc22a8-0297-4380-896a-58e0a4d64946"),sQuery(id+"F0.wireOp",EDGE,"2896c270-dc6a-46f7-af7e-f09f457604b9"),sQuery(id+"F0.wireOp",EDGE,"f6aba6df-df45-4b05-993e-c7defc46a8a9"),sQuery(id+"F0.wireOp",EDGE,"8d709430-df8d-444d-80f1-d8a9d8f49d36"),sQuery(id+"F0.wireOp",EDGE,"157fc770-0e9c-4f22-853e-0631539bb4e1"),sQuery(id+"F0.wireOp",EDGE,"a9f1098b-83a8-4a87-b43b-ebdedd82ef22"),sQuery(id+"F0.wireOp",EDGE,"aa613513-3a1a-4f7c-8e9e-b6ef198c339f"),sQuery(id+"F0.wireOp",EDGE,"fe532b5b-20c2-4205-9ddd-15005d39a7ff"),sQuery(id+"F0.wireOp",EDGE,"65eb4da6-f79f-4cfa-8aa6-be833dba4871"),sQuery(id+"F0.wireOp",EDGE,"c5a74e05-6458-4890-878c-c1706ed33956"),sQuery(id+"F0.wireOp",EDGE,"496d6b06-fe4e-4fad-814f-3270d9f86b10"),sQuery(id+"F0.wireOp",EDGE,"e228dba5-c171-4fc2-b486-8333351927fa"),sQuery(id+"F0.wireOp",EDGE,"d01ee6cb-36a2-45a1-89ac-166ec7de60b6"),sQuery(id+"F0.wireOp",EDGE,"E3"),sQuery(id+"F0.wireOp",EDGE,"E4"),sQuery(id+"F0.wireOp",EDGE,"436595a8-e4a6-4182-82a2-6fdc5edbe3d4"),sQuery(id+"F0.wireOp",EDGE,"6fa8d768-685f-4659-b18a-b4b0655affab"),sQuery(id+"F0.wireOp",EDGE,"3112937d-f164-4bee-b1b8-f487c5c27332"),sQuery(id+"F0.wireOp",EDGE,"2838ab75-a7b3-46be-88fa-19408c43f44a"),sQuery(id+"F0.wireOp",EDGE,"4df78863-24a2-4663-8bca-78eb0f9ee46f"),sQuery(id+"F0.wireOp",EDGE,"76a8d0a0-a03e-4017-96cb-accdf860527a"),sQuery(id+"F0.wireOp",EDGE,"d24411e6-fbae-4226-8ade-65dde889be9d"),sQuery(id+"F0.wireOp",EDGE,"bc01f53f-b851-4eac-bdc6-b53b8c4c76a6"),sQuery(id+"F0.wireOp",EDGE,"69d3b90a-bc34-4f77-bf78-b3aee6b0a92d"),sQuery(id+"F0.wireOp",EDGE,"373f017d-76e3-442f-9662-ada9d0238173"),sQuery(id+"F0.wireOp",EDGE,"E5"),sQuery(id+"F0.wireOp",EDGE,"E6"),sQuery(id+"F0.wireOp",EDGE,"E7"),sQuery(id+"F0.wireOp",EDGE,"2cd16a8c-3307-4928-bd26-f5d255e7399a"),sQuery(id+"F0.wireOp",EDGE,"193ac13c-8e04-4e5c-91c6-e2d340e07c24"),sQuery(id+"F0.wireOp",EDGE,"6f13a96e-32fe-4fc2-9d82-1492d29b6e04"),sQuery(id+"F0.wireOp",EDGE,"fc8c22b4-d4e1-4527-bd38-377e5530003c"),sQuery(id+"F0.wireOp",EDGE,"4d59d710-4fe3-4597-a13d-8c3004e22d5d"),sQuery(id+"F0.wireOp",EDGE,"29ced08f-bc4c-4871-942e-da1849301c59"),sQuery(id+"F0.wireOp",EDGE,"5d328fcf-ca32-4b9a-8d95-4cec8a7c74f5"),sQuery(id+"F0.wireOp",EDGE,"I1ITQqyg-hlTV-tP51-8M3V-AqXVVhc1bbyB"),sQuery(id+"F0.wireOp",EDGE,"Ww1sCOVc-raFa-45lX-seSL-zmaeCrGf7sdz")])],"isStart":true});
            extrude(context, id + "F3", {"entities" : qUnion([Q0]), "operationType" : NewBodyOperationType.ADD, "endBound" : BoundingType.UP_TO_SURFACE, "oppositeDirection" : true, "depth" : 25 * mm, "endBoundEntityFace" : qUnion([Q1]), "offsetDistance" : 25 * mm});
        }
        {
            var Q0;
            Q0=makeQuery(id+"F3.boolean.opBoolean","MERGE",FACE,{"derivedFrom":[makeQuery(id+"F1.opExtrude","CAP_FACE",FACE,{"disambiguationData":[OSD([sQuery(id+"F0.wireOp",EDGE,"E0"),sQuery(id+"F0.wireOp",EDGE,"48a6f060-a1ac-46d0-8047-a4f0a9823539"),sQuery(id+"F0.wireOp",EDGE,"E1"),sQuery(id+"F0.wireOp",EDGE,"E2"),sQuery(id+"F0.wireOp",EDGE,"f30ca258-66be-4d38-bb74-7f78c57f1080"),sQuery(id+"F0.wireOp",EDGE,"45272e1f-5984-409b-a4f0-3096130aef37"),sQuery(id+"F0.wireOp",EDGE,"648265e5-3534-4ccd-a4d5-83f80079090c"),sQuery(id+"F0.wireOp",EDGE,"c0985e6e-a1f7-4fb3-8751-1b5ac6839632"),sQuery(id+"F0.wireOp",EDGE,"e40d4cf7-7397-40ef-a449-90f8d66566dd"),sQuery(id+"F0.wireOp",EDGE,"e08eb2a6-f8ba-4677-9665-afa96b0a5c42"),sQuery(id+"F0.wireOp",EDGE,"e09e89fb-475b-45c4-a03c-8bf25691b274"),sQuery(id+"F0.wireOp",EDGE,"c3a1d90c-5dae-4514-9c18-9578f9fa1c24"),sQuery(id+"F0.wireOp",EDGE,"de0bfc80-6dc8-401c-842a-22218dc18f48"),sQuery(id+"F0.wireOp",EDGE,"10bace14-cf57-4a17-8dbc-91b2d8cd16bf"),sQuery(id+"F0.wireOp",EDGE,"deb3eb6b-2df6-45dd-ab49-f1686ca42383"),sQuery(id+"F0.wireOp",EDGE,"6de70d99-d249-41b2-88aa-bb0862796ce5"),sQuery(id+"F0.wireOp",EDGE,"b2971fcf-4c8f-4d95-a7b3-968699cf8065"),sQuery(id+"F0.wireOp",EDGE,"79488e33-7403-455a-a2d1-9183c7a7dc75"),sQuery(id+"F0.wireOp",EDGE,"aa5a9b35-dc5f-46a3-a21f-bc2f6a5ba8c3"),sQuery(id+"F0.wireOp",EDGE,"64001aba-4a60-4bdb-a6e0-b909cfa90190"),sQuery(id+"F0.wireOp",EDGE,"69a3c832-ee76-48c3-8be5-449944f03f95"),sQuery(id+"F0.wireOp",EDGE,"49a81c46-1861-4f30-adb0-815aeb534458"),sQuery(id+"F0.wireOp",EDGE,"e41367db-3de3-4109-90ef-63e5f0f7b1f7"),sQuery(id+"F0.wireOp",EDGE,"6e4c30f9-b3e7-4410-98fe-95563731d562"),sQuery(id+"F0.wireOp",EDGE,"50d6a7da-0eb8-46df-9db0-2777529e0e33"),sQuery(id+"F0.wireOp",EDGE,"8f5f6bae-5651-4266-a81d-530af63d2ea9"),sQuery(id+"F0.wireOp",EDGE,"0c91ba03-d5dc-41c7-8701-761e688114d9"),sQuery(id+"F0.wireOp",EDGE,"10e95849-eba9-4293-a9a6-05e2b37bbdfd"),sQuery(id+"F0.wireOp",EDGE,"edf70701-9639-44fa-8111-f0ba9ba4bb0e"),sQuery(id+"F0.wireOp",EDGE,"9cb7c61f-063f-4e49-a479-e91a873714ef"),sQuery(id+"F0.wireOp",EDGE,"23d4df54-0a09-4bbe-b8b9-fc41ac67f4ac"),sQuery(id+"F0.wireOp",EDGE,"d0cc7293-f9a2-43ae-ac4b-742a364b32c0"),sQuery(id+"F0.wireOp",EDGE,"1dbc8700-6e9f-4588-83ba-0a038fd47aa9"),sQuery(id+"F0.wireOp",EDGE,"171cbcd0-81c7-4dfe-8efe-28eec8b9f1e2"),sQuery(id+"F0.wireOp",EDGE,"1b840b68-42d4-491e-8676-f044272edf1d"),sQuery(id+"F0.wireOp",EDGE,"477a06df-0e00-41ca-87d7-5c34f2a07242"),sQuery(id+"F0.wireOp",EDGE,"7aeb2e31-d47a-4962-ad1a-87ad22c54afe"),sQuery(id+"F0.wireOp",EDGE,"8aeabe10-1c55-41c1-b53d-efc54e2343e8"),sQuery(id+"F0.wireOp",EDGE,"56056688-4674-4c79-9f3a-c66bce5d7240"),sQuery(id+"F0.wireOp",EDGE,"2ba6e904-2303-4a58-a2cc-d8b69b776228"),sQuery(id+"F0.wireOp",EDGE,"5e924ffd-c203-416b-82ef-407f079c669c"),sQuery(id+"F0.wireOp",EDGE,"22999e4d-675b-4f8e-a222-469bac07e6be"),sQuery(id+"F0.wireOp",EDGE,"8f11fb03-c33d-4eef-9f43-5a4f08b6129f"),sQuery(id+"F0.wireOp",EDGE,"a5862e19-85fe-4436-8071-eee2bcb2075c"),sQuery(id+"F0.wireOp",EDGE,"ed11b90d-34d2-40d8-97b3-85c497fa4b90"),sQuery(id+"F0.wireOp",EDGE,"8821150d-f62d-464a-944b-e17730e76b97"),sQuery(id+"F0.wireOp",EDGE,"73421591-e8bf-419b-8db1-77e700152255"),sQuery(id+"F0.wireOp",EDGE,"55a8d366-2669-4621-9984-ea7371f670e7"),sQuery(id+"F0.wireOp",EDGE,"fca3974c-c5bd-4598-b391-3bcec77630d6"),sQuery(id+"F0.wireOp",EDGE,"1c73d825-d1c4-4b0e-8cd0-2f197b32ed0e"),sQuery(id+"F0.wireOp",EDGE,"f12474dd-ca9d-467a-b6b7-96876f0ada5b"),sQuery(id+"F0.wireOp",EDGE,"ffd498c9-8f44-4c4b-88ae-d53ebce42681"),sQuery(id+"F0.wireOp",EDGE,"d78736cb-32b1-4983-8c7f-334d7760df66"),sQuery(id+"F0.wireOp",EDGE,"95740ca0-fcd5-4cb7-9504-a285a5dde6e3"),sQuery(id+"F0.wireOp",EDGE,"ebb5eec3-1149-4952-a6d1-94870ff9836f"),sQuery(id+"F0.wireOp",EDGE,"09364745-caed-4ffe-8d3c-952926bc9417"),sQuery(id+"F0.wireOp",EDGE,"a9181265-9252-4b23-9b63-f6bef6a5911b"),sQuery(id+"F0.wireOp",EDGE,"a53fe2a5-8e1d-4d15-8c4a-13980fa5923c"),sQuery(id+"F0.wireOp",EDGE,"9b227ee3-73b3-485d-a44c-8cd02b23a3f0"),sQuery(id+"F0.wireOp",EDGE,"062db7e1-9f89-4046-92a1-9e257b0f6c50"),sQuery(id+"F0.wireOp",EDGE,"351c1721-7ed2-435b-ad4a-6d0b63d51eff"),sQuery(id+"F0.wireOp",EDGE,"71a8f4bf-e319-473b-8b4e-3c091c66e44c"),sQuery(id+"F0.wireOp",EDGE,"c68ce1a5-2e28-4d52-a029-c52856a99a74"),sQuery(id+"F0.wireOp",EDGE,"561223bc-eb1b-49aa-80b6-663cd7c405cc"),sQuery(id+"F0.wireOp",EDGE,"4449a819-5709-48c0-965c-65add78f8043"),sQuery(id+"F0.wireOp",EDGE,"a0f13820-d3c8-4b17-b0b8-00fd948fe85f"),sQuery(id+"F0.wireOp",EDGE,"20fca5f8-8561-4aa7-a30f-3738d70a8836"),sQuery(id+"F0.wireOp",EDGE,"920726d8-d7a8-4d7b-bd5a-44d794fb4a9e"),sQuery(id+"F0.wireOp",EDGE,"a76c174e-0144-4079-be69-9e1200ad9bf8"),sQuery(id+"F0.wireOp",EDGE,"98b53387-61df-4284-a1fd-1e532390bc76"),sQuery(id+"F0.wireOp",EDGE,"7970af7d-46bf-4ec9-b671-f062ccba2269"),sQuery(id+"F0.wireOp",EDGE,"6e09d304-04a0-4725-848f-3effe17a6afc"),sQuery(id+"F0.wireOp",EDGE,"3df50d65-f073-4170-bc94-899382cb2db7"),sQuery(id+"F0.wireOp",EDGE,"ec83f8f2-8803-4207-88f9-0d4175c8ecd2"),sQuery(id+"F0.wireOp",EDGE,"2f88a13a-97f7-4f31-871f-ef8b0bef47c0"),sQuery(id+"F0.wireOp",EDGE,"06910b89-3a32-40f6-98a8-ac0792bcf854"),sQuery(id+"F0.wireOp",EDGE,"1496428c-a744-4ad0-9076-c4c48af7c995"),sQuery(id+"F0.wireOp",EDGE,"cc24b7ec-eed3-4d97-bc37-77a5319da4e8"),sQuery(id+"F0.wireOp",EDGE,"f009715c-78f4-41d5-a120-40e9715128f4"),sQuery(id+"F0.wireOp",EDGE,"5595ca81-0dc4-4751-825f-2c64607c6bfd"),sQuery(id+"F0.wireOp",EDGE,"75137ea1-8823-43c0-92ee-8dea83bb2410"),sQuery(id+"F0.wireOp",EDGE,"f83aa6e6-86ae-462f-9473-6b6f0fb29268"),sQuery(id+"F0.wireOp",EDGE,"d90fdb54-86cb-4136-93d7-04ef30efafac"),sQuery(id+"F0.wireOp",EDGE,"8bd12bbf-22fc-44f8-9b72-60e51806dfd9"),sQuery(id+"F0.wireOp",EDGE,"d2235da4-86d1-4fb2-9421-07340d50dd9e"),sQuery(id+"F0.wireOp",EDGE,"63672669-45e7-48f5-b998-5c0e149c1244"),sQuery(id+"F0.wireOp",EDGE,"58c0fe2c-0100-4913-a047-5c3918bec01d"),sQuery(id+"F0.wireOp",EDGE,"41e70165-0540-472b-ae5f-d4663d4ebe0f"),sQuery(id+"F0.wireOp",EDGE,"6970c7cc-29ee-40f8-b0b1-14e57c32c814"),sQuery(id+"F0.wireOp",EDGE,"349e1bc8-b4a3-4d58-8a14-12c9859b9f7c"),sQuery(id+"F0.wireOp",EDGE,"87991a84-08ac-46d3-90c5-f5fa6d0c5a83"),sQuery(id+"F0.wireOp",EDGE,"d48f1f7f-ed81-45d4-8615-b0910d7520c1"),sQuery(id+"F0.wireOp",EDGE,"7e9c43bc-bf7d-4118-b5fc-4f360d9f3191"),sQuery(id+"F0.wireOp",EDGE,"2759085c-90ad-42ab-8a63-b83350e672f3"),sQuery(id+"F0.wireOp",EDGE,"39805100-74d7-4eed-b193-147db33826ff"),sQuery(id+"F0.wireOp",EDGE,"6fa17770-5563-4e58-b27d-c8ec50f6b9eb"),sQuery(id+"F0.wireOp",EDGE,"32f67bb0-8620-4629-98bb-09f92e1a7203"),sQuery(id+"F0.wireOp",EDGE,"1ab79bf1-ba5c-4050-a713-1e5aa506e06c"),sQuery(id+"F0.wireOp",EDGE,"ffed6f08-e811-4981-a8fd-a7a3ecd42359"),sQuery(id+"F0.wireOp",EDGE,"2f2290aa-816a-4cc3-8e39-136d9264129f"),sQuery(id+"F0.wireOp",EDGE,"b78c8009-cc0b-41b3-a308-2ea56fda7653"),sQuery(id+"F0.wireOp",EDGE,"19267ec7-4eb6-4897-a0c4-8a92806a641a"),sQuery(id+"F0.wireOp",EDGE,"d0838ca9-0bd1-4f24-9d56-d46021ac47bb"),sQuery(id+"F0.wireOp",EDGE,"ce547bf3-1506-4fd9-949b-1fb36aabb9ca"),sQuery(id+"F0.wireOp",EDGE,"e414b3ae-820b-420c-b87e-729e0b5eba94"),sQuery(id+"F0.wireOp",EDGE,"edeb106c-0092-4fe6-b9c2-1a1c4f8eb62e"),sQuery(id+"F0.wireOp",EDGE,"c81b4543-384f-45e1-8dd5-319bf77e4dd3"),sQuery(id+"F0.wireOp",EDGE,"46d69cc5-4e9e-43d0-9594-28f258b2da8d"),sQuery(id+"F0.wireOp",EDGE,"0f81ca49-7ceb-4d09-8dc9-9a04f8bc6888"),sQuery(id+"F0.wireOp",EDGE,"b58b9564-60eb-4c8a-b30f-9b977b1b8378"),sQuery(id+"F0.wireOp",EDGE,"d8bbd356-4e6d-4438-af8e-85043a16574a"),sQuery(id+"F0.wireOp",EDGE,"95fa0bd5-89c6-4184-a0ff-f4c07d22a4ae"),sQuery(id+"F0.wireOp",EDGE,"f4548e74-734f-430b-9c25-dfe130f893d1"),sQuery(id+"F0.wireOp",EDGE,"aa9bd5ec-27bf-46b3-b434-4e99c0207ced"),sQuery(id+"F0.wireOp",EDGE,"9be34343-3f5a-40f5-8c55-a74b86983d61"),sQuery(id+"F0.wireOp",EDGE,"78e4d226-de00-4f6e-ab81-cb0a13cdacba"),sQuery(id+"F0.wireOp",EDGE,"3a4dbe18-ff8c-426a-b249-17c5fc8cdc1d"),sQuery(id+"F0.wireOp",EDGE,"1aed8480-7217-479a-a0ab-f2862b378fde"),sQuery(id+"F0.wireOp",EDGE,"b4489634-a053-4e93-951f-f30401c3c6f6"),sQuery(id+"F0.wireOp",EDGE,"cc371cea-5bb3-4e27-997b-0d34cdc5a024"),sQuery(id+"F0.wireOp",EDGE,"86368e5d-c637-4ae6-8edd-554a0b5499c9"),sQuery(id+"F0.wireOp",EDGE,"13f25098-72eb-41f9-be21-613ca2679d4b"),sQuery(id+"F0.wireOp",EDGE,"1f474f0c-89c3-40ee-8296-02d5ac8c763d"),sQuery(id+"F0.wireOp",EDGE,"13320aed-ccdc-4340-973a-86da583243d3"),sQuery(id+"F0.wireOp",EDGE,"0f343cd8-6904-487c-9847-16acd28769b1"),sQuery(id+"F0.wireOp",EDGE,"f8d5171c-c807-4338-b4d2-ff111a4d6950"),sQuery(id+"F0.wireOp",EDGE,"531f2c4b-3846-4b77-b256-c3f1f96e1e9d"),sQuery(id+"F0.wireOp",EDGE,"f1731d2a-7704-4802-8ffe-e10816912d59"),sQuery(id+"F0.wireOp",EDGE,"663e4867-d1df-44f6-8d72-edf692fa190b"),sQuery(id+"F0.wireOp",EDGE,"ab6ac0ee-4fb0-40ab-99bd-49c6310301f1"),sQuery(id+"F0.wireOp",EDGE,"020361ae-c990-440f-b82b-d8defa8b7b3c"),sQuery(id+"F0.wireOp",EDGE,"f234d57d-ff2e-4084-99c6-6c5da22014f4"),sQuery(id+"F0.wireOp",EDGE,"5704d1bf-8f80-4d6a-bd46-ef1de08cc11a"),sQuery(id+"F0.wireOp",EDGE,"49977618-c097-4a49-a1ed-c88bfdf155e3"),sQuery(id+"F0.wireOp",EDGE,"ba9d945f-4033-4ba8-a865-6404f0a478a9"),sQuery(id+"F0.wireOp",EDGE,"c57414d4-a29c-435f-b64d-f2822a14b6a6"),sQuery(id+"F0.wireOp",EDGE,"be5730e7-9658-4d88-be84-16e7c03488bd"),sQuery(id+"F0.wireOp",EDGE,"a75bae47-d3a2-4152-ab54-74ed0c49e5a7"),sQuery(id+"F0.wireOp",EDGE,"6e3ff476-3da9-4782-8826-f396f37c11b6"),sQuery(id+"F0.wireOp",EDGE,"05769db6-19a1-4fe3-98a5-9d1978582ff3"),sQuery(id+"F0.wireOp",EDGE,"5dad99bb-ebf8-4bc1-8dc4-4c0a6e99aceb"),sQuery(id+"F0.wireOp",EDGE,"c816ae48-71c4-4d0e-8c30-5d1046f78968"),sQuery(id+"F0.wireOp",EDGE,"cfd27d30-f5e3-48dc-9665-aa6919d9858b"),sQuery(id+"F0.wireOp",EDGE,"4725fb37-e1ea-4f57-b98a-89feef752827"),sQuery(id+"F0.wireOp",EDGE,"ae6adbf3-7d98-4c9e-8eb2-f79f6d337834"),sQuery(id+"F0.wireOp",EDGE,"640fbc53-f186-4556-84a7-69dc03839d6f"),sQuery(id+"F0.wireOp",EDGE,"e1422021-42bf-4d48-97a0-4a21d4969dc9"),sQuery(id+"F0.wireOp",EDGE,"c074cf32-69e8-4938-8c1f-45b8d0bb0a1c"),sQuery(id+"F0.wireOp",EDGE,"a8cc22a8-0297-4380-896a-58e0a4d64946"),sQuery(id+"F0.wireOp",EDGE,"2896c270-dc6a-46f7-af7e-f09f457604b9"),sQuery(id+"F0.wireOp",EDGE,"f6aba6df-df45-4b05-993e-c7defc46a8a9"),sQuery(id+"F0.wireOp",EDGE,"8d709430-df8d-444d-80f1-d8a9d8f49d36"),sQuery(id+"F0.wireOp",EDGE,"157fc770-0e9c-4f22-853e-0631539bb4e1"),sQuery(id+"F0.wireOp",EDGE,"a9f1098b-83a8-4a87-b43b-ebdedd82ef22"),sQuery(id+"F0.wireOp",EDGE,"aa613513-3a1a-4f7c-8e9e-b6ef198c339f"),sQuery(id+"F0.wireOp",EDGE,"fe532b5b-20c2-4205-9ddd-15005d39a7ff"),sQuery(id+"F0.wireOp",EDGE,"65eb4da6-f79f-4cfa-8aa6-be833dba4871"),sQuery(id+"F0.wireOp",EDGE,"c5a74e05-6458-4890-878c-c1706ed33956"),sQuery(id+"F0.wireOp",EDGE,"496d6b06-fe4e-4fad-814f-3270d9f86b10"),sQuery(id+"F0.wireOp",EDGE,"e228dba5-c171-4fc2-b486-8333351927fa"),sQuery(id+"F0.wireOp",EDGE,"d01ee6cb-36a2-45a1-89ac-166ec7de60b6"),sQuery(id+"F0.wireOp",EDGE,"E3"),sQuery(id+"F0.wireOp",EDGE,"E4"),sQuery(id+"F0.wireOp",EDGE,"436595a8-e4a6-4182-82a2-6fdc5edbe3d4"),sQuery(id+"F0.wireOp",EDGE,"6fa8d768-685f-4659-b18a-b4b0655affab"),sQuery(id+"F0.wireOp",EDGE,"3112937d-f164-4bee-b1b8-f487c5c27332"),sQuery(id+"F0.wireOp",EDGE,"2838ab75-a7b3-46be-88fa-19408c43f44a"),sQuery(id+"F0.wireOp",EDGE,"4df78863-24a2-4663-8bca-78eb0f9ee46f"),sQuery(id+"F0.wireOp",EDGE,"76a8d0a0-a03e-4017-96cb-accdf860527a"),sQuery(id+"F0.wireOp",EDGE,"d24411e6-fbae-4226-8ade-65dde889be9d"),sQuery(id+"F0.wireOp",EDGE,"bc01f53f-b851-4eac-bdc6-b53b8c4c76a6"),sQuery(id+"F0.wireOp",EDGE,"69d3b90a-bc34-4f77-bf78-b3aee6b0a92d"),sQuery(id+"F0.wireOp",EDGE,"373f017d-76e3-442f-9662-ada9d0238173"),sQuery(id+"F0.wireOp",EDGE,"E5"),sQuery(id+"F0.wireOp",EDGE,"E6"),sQuery(id+"F0.wireOp",EDGE,"E7"),sQuery(id+"F0.wireOp",EDGE,"2cd16a8c-3307-4928-bd26-f5d255e7399a"),sQuery(id+"F0.wireOp",EDGE,"193ac13c-8e04-4e5c-91c6-e2d340e07c24"),sQuery(id+"F0.wireOp",EDGE,"6f13a96e-32fe-4fc2-9d82-1492d29b6e04"),sQuery(id+"F0.wireOp",EDGE,"fc8c22b4-d4e1-4527-bd38-377e5530003c"),sQuery(id+"F0.wireOp",EDGE,"4d59d710-4fe3-4597-a13d-8c3004e22d5d"),sQuery(id+"F0.wireOp",EDGE,"29ced08f-bc4c-4871-942e-da1849301c59"),sQuery(id+"F0.wireOp",EDGE,"5d328fcf-ca32-4b9a-8d95-4cec8a7c74f5"),sQuery(id+"F0.wireOp",EDGE,"I1ITQqyg-hlTV-tP51-8M3V-AqXVVhc1bbyB"),sQuery(id+"F0.wireOp",EDGE,"Ww1sCOVc-raFa-45lX-seSL-zmaeCrGf7sdz")])],"isStart":false}),makeQuery(id+"F3.opExtrude","CAP_FACE",FACE,{"disambiguationData":[OSD([sQuery(id+"F2.wireOp",EDGE,"E12.bottom"),sQuery(id+"F2.wireOp",EDGE,"E12.top"),sQuery(id+"F2.wireOp",EDGE,"E12.left"),sQuery(id+"F2.wireOp",EDGE,"E12.right"),sQuery(id+"F2.wireOp",EDGE,"E13.filletArc"),sQuery(id+"F2.wireOp",EDGE,"E14.filletArc")])],"isStart":true})]});
            var sketch = newSketch(context, id + "F4", { "sketchPlane" : qUnion([Q0])});
            skText(sketch, "E15", { "text": "DL650", "fontName": "RobotoSlab-Bold.ttf"});
            const initialGuessF4  = {"E15": [0.00441, -0.053, 1, 0, 0.015]};
            skSetInitialGuess(sketch, initialGuessF4);
            skSolve(sketch);
        }
        {
            var Q0;
            Q0=qSketchRegion(id+"F4",true);
            extrude(context, id + "F5", {"entities" : qUnion([Q0]), "operationType" : NewBodyOperationType.ADD, "depth" : .8 * mm, "offsetDistance" : 25 * mm});
        }
        {
            var Q0;
            {var subQ0=sQuery(id+"F0.wireOp",EDGE,"E6");var subQ1=sQuery(id+"F0.wireOp",EDGE,"E5");var subQ2=sQuery(id+"F0.wireOp",EDGE,"E4");var subQ3=sQuery(id+"F0.wireOp",EDGE,"E3");var subQ4=sQuery(id+"F0.wireOp",EDGE,"E2");var subQ5=sQuery(id+"F0.wireOp",EDGE,"E1");var subQ6=sQuery(id+"F0.wireOp",EDGE,"E0");var subQ7=sQuery(id+"F2.wireOp",EDGE,"E12.left");var subQ8=sQuery(id+"F2.wireOp",EDGE,"E12.top");var subQ9=sQuery(id+"F2.wireOp",EDGE,"E12.right");var subQ10=sQuery(id+"F2.wireOp",EDGE,"E13.filletArc");var subQ11=sQuery(id+"F2.wireOp",EDGE,"E14.filletArc");Q0=makeQuery(id+"F5.boolean.opBoolean","SPLIT",FACE,{"disambiguationData":[TD([makeQuery(id+"F1.opExtrude","SWEPT_FACE",FACE,{"disambiguationData":[OSD([subQ6])]})])],"derivedFrom":makeQuery(id+"F3.boolean.opBoolean","MERGE",FACE,{"derivedFrom":[makeQuery(id+"F1.opExtrude","CAP_FACE",FACE,{"disambiguationData":[OSD([subQ6,subQ5,subQ4,subQ3,subQ2,subQ1,subQ0,sQuery(id+"F0.wireOp",EDGE,"E7"),sQuery(id+"F0.wireOp",EDGE,"4d59d710-4fe3-4597-a13d-8c3004e22d5d"),sQuery(id+"F0.wireOp",EDGE,"29ced08f-bc4c-4871-942e-da1849301c59"),sQuery(id+"F0.wireOp",EDGE,"2gHOES4c-l3Kz-l0sa-6fCd-MSWam39DBxH3"),sQuery(id+"F0.wireOp",EDGE,"33JrRZkF-bzf7-lZC0-NyB4-XBJtuySfmqfx")])],"isStart":false}),makeQuery(id+"F3.opExtrude","CAP_FACE",FACE,{"disambiguationData":[OSD([sQuery(id+"F2.wireOp",EDGE,"E12.bottom"),subQ8,subQ7,subQ9,subQ10,subQ11])],"isStart":true})]})});}
            var sketch = newSketch(context, id + "F6", { "sketchPlane" : qUnion([Q0])});
            skLineSegment(sketch, "E16.bottom", {"start": v(-88, 72.5) * mm, "end": v(88, 72.5) * mm});
            skLineSegment(sketch, "E16.top", {"start": v(-91, -36) * mm, "end": v(91, -36) * mm});
            skLineSegment(sketch, "E16.left", {"start": v(-91, 69.5) * mm, "end": v(-91, -36) * mm});
            skLineSegment(sketch, "E16.right", {"start": v(91, 69.5) * mm, "end": v(91, -36) * mm});
            skLineSegment(sketch, "E17", {"start": v(0, 0) * mm, "end": v(0, 27.2) * mm, "construction": true});
            skLineSegment(sketch, "E18", {"start": v(0, 27.2) * mm, "end": v(-91, 27.2) * mm, "construction": true});
            skLineSegment(sketch, "E19", {"start": v(0, 27.2) * mm, "end": v(91, 27.2) * mm, "construction": true});
            skLineSegment(sketch, "E20", {"start": v(-68.26, 60) * mm, "end": v(-48.63, 60) * mm, "construction": true});
            skPoint(sketch, "E21.visualSharp", {"position": v(-91, 72.5) * mm});
            skArc(sketch, "E21.filletArc", {"start": v(-88, 72.5) * mm, "mid": v(-90.12, 71.62) * mm, "end": v(-91, 69.5) * mm});
            skPoint(sketch, "E22.visualSharp", {"position": v(91, 72.5) * mm});
            skArc(sketch, "E22.filletArc", {"start": v(91, 69.5) * mm, "mid": v(90.12, 71.62) * mm, "end": v(88, 72.5) * mm});
            skSolve(sketch);
        }
        {
            var Q0;
            Q0 = qSketchRegion(id + "F6", true);
            extrude(context, id + "F7", {"entities" : qUnion([Q0]), "operationType" : NewBodyOperationType.REMOVE, "oppositeDirection" : true, "depth" : 1.4 * mm, "offsetDistance" : 25 * mm});
        }
    });
